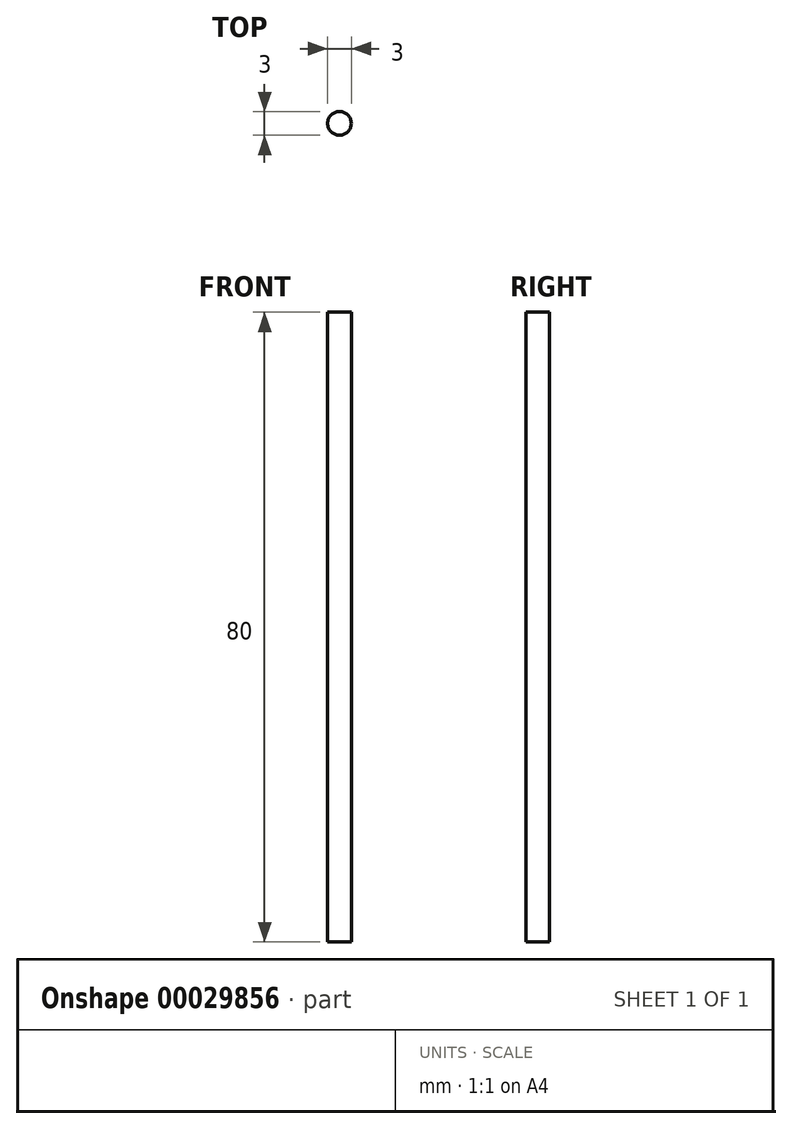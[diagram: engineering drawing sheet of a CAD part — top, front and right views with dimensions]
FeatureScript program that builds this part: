
annotation { "Feature Type Name" : "Feature", "Feature Type Description" : "" }
export const myFeature = defineFeature(function(context is Context, id is Id, definition is map)
    precondition{}
    {
        {
            var Q0;
            Q0=qCreatedBy(makeId("Top.planeOp"),FACE);
            var sketch = newSketch(context, id + "F0", { "sketchPlane" : qUnion([Q0])});
            skCircle(sketch, "E0", {"center": v(0, 0) * mm, "radius": 1.5 * mm});
            skSolve(sketch);
        }
        {
            var Q0;
            Q0=makeQuery(id+"F0.imprint","IMPRINT",FACE,{"disambiguationData":[TD([[makeQuery(id+"F0.imprint","IMPRINT",EDGE,{"derivedFrom":sQuery(id+"F0.wireOp",EDGE,"E0")}),1.0]])]});
            extrude(context, id + "F1", {"entities" : qUnion([Q0]), "depth" : 40 * mm, "hasSecondDirection" : true, "secondDirectionOppositeDirection" : true, "secondDirectionDepth" : 40 * mm});
        }
    });
